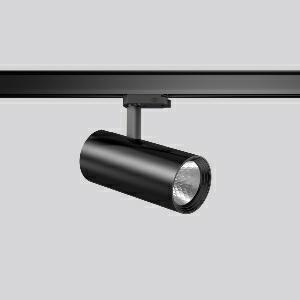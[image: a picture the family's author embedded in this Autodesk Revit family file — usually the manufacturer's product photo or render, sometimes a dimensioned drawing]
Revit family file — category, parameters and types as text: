
# Revit family: deecos_s_mini_742197_003_1_76_d194
name_source: partatom
category: Lighting Fixtures
units: mm (PartAtom-declared; Revit-internal decimal feet)

## family parameters
Cut with Voids When Loaded = No
Host = Face
Light Source = No
Part Type = Normal
Room Calculation Point = No
Round Connector Dimension = Use Diameter
Shared = No

## types (1)
- DEECOS S mini (1 x LED Modul 940, 2750 lm, 4000)
    Apparent Load = 20 VA
    Approval mark = CE
    CIE Flux Codes = 95 99 100 100 100
    Color Rendering = 92
    Color Temperature = 4000
    Default Elevation = 1800 mm
    Description = Series: DEECOS S mini
LED surface-mounted projector in modern design with no visible cooling ribs. Housing: die-cast aluminium, powder-coated. Rotation range: 356°. Swivel range: 90°. Black plastic ring and recessed LED to prevent glare from the side. Optical assembly with reflector made of MIRO-Silver with 98% total light reflection for outstanding efficiency - can be changed without tools. Best colour rendering index Ra>90. With adapter for RZB 3-circuit DALI tracks. Suitable for Track on ceiling, Wall track. High quality converter without flickering and stroboscopic effect. The following accessories can be mounted without use of tools: interchangeable lenses, decorative glasses, honeycomb louvre, clear and frosted diffusers, white interchangeable plastic ring. 
Colour: deep black, matt (RAL 9005)
Diameter: 87 mm
Height: 214 mm
Lamp: LED
Socket: without socket
Colour temperature: 4000K
Colour rendering index (CRI): 92
System power: 20 W
Rated luminous flux: 2750 lm
Luminous efficiency: 138 lm/W
Control gear: Converter, dimmable, DALI
Protection class: I
Type of protection: IP 20
    Height = 214 mm
    Lamp = 1 x LED Modul 940
    Lamp Light Flux = 2750 lm
    Lamp count = 1
    Length = 87 mm
    Lifetime = 50000 h
    Luminous efficacy = 138 lm/W
    Manufacturer = RZB
    ModVariant = No
    Model = 742197.003.1.76
    Mounting Place = Ceiling
    Mounting Type = Rail mounted
    Number of Poles = 1
    OnlyDefault = Yes
    Power Factor = 1
    Product Name = DEECOS S mini
    Product group = Track mounted projectors
    ProductGroupID = 301
    Protection Class = Protection class I
    Protection Degree = IP 20
    RLX_Detail_Level = 1
    RLX_Emergency_Light_Flux = 0 lm
    RLX_Emergency_Type = 0
    RLX_Emergency_Type_DB = No
    RlxData = <blob elided: 38953 chars, md5=0ec0ee1f>
    Socket = socket
    Standby Power = 0 W
    System Light Flux = 2750 lm
    System Power = 20 W
    Type Comments = Product without accessories
    Type Image = 741926.003.jpg
    URL = http://relux.com
    VarID = ---
    Voltage = 230 V
    Voltage Range = 220-240 V
    Weight = 0.00 kg
    Width = 0 mm  [stored 0 ft]

note: [stored X ft] marks values corroborated as IEEE doubles in the binary element streams (Revit-internal decimal feet)

## geometry (parser evidence)
native form markers: Blend x4, Sweep x10
no freeform markers — native parametric forms only
